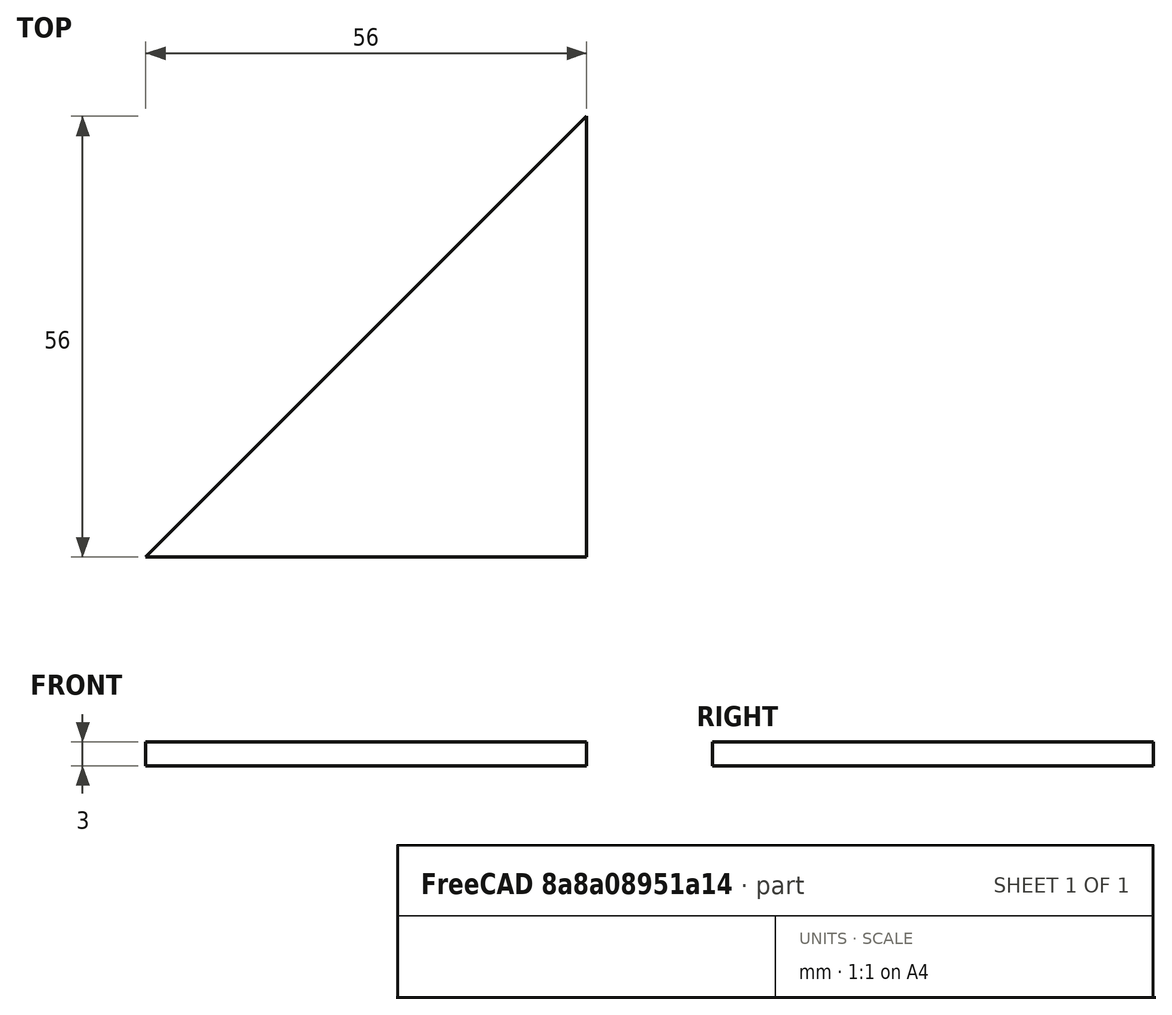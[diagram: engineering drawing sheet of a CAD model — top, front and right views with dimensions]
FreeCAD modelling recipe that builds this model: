
FCSTD DOCUMENT  (FreeCAD 0.19R24276 (Git))
Label: Nemo23_support_side
License: All rights reserved
LicenseURL: http://en.wikipedia.org/wiki/All_rights_reserved
objects: Sketcher::SketchObject×1, PartDesign::Pad×1, PartDesign::Body×1
note: 4 computed .brp shape members not serialized (recipe doc carries the construction recipe); baked Part::Feature solids carry a one-line shape summary decoded from their .brp

FEATURE [Sketcher::SketchObject] Sketch
  FullyConstrained = true
  MapMode = 5
  Support = -> [XY_Plane]
  sketch-geometry (3):
    g0: LineSegment StartX=0 StartY=-7.1e-15 StartZ=0 EndX=-56 EndY=-7.1e-15 EndZ=0
    g1: LineSegment StartX=0 StartY=-7.1e-15 StartZ=0 EndX=0 EndY=56 EndZ=0
    g2: LineSegment StartX=0 StartY=56 StartZ=0 EndX=-56 EndY=-7.1e-15 EndZ=0
  constraints (8):
    c: Coincident(g0,g-1)
    c: Horizontal(g0)
    c: Coincident(g1,g0)
    c: PointOnObject(g1,g-2)
    c: Coincident(g2,g1)
    c: Coincident(g2,g0)
    c: DistanceY(g1,g1) = 56
    c: DistanceX(g0,g0) = 56
FEATURE [PartDesign::Pad] Pad
  Direction = (1,1,1)
  Length = 3
  Length2 = 100
  Profile = -> Sketch
  Type = 0
FEATURE [PartDesign::Body] Body
  Group = -> [Sketch,Pad]
  Origin = -> Origin
  Tip = -> Pad
